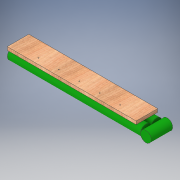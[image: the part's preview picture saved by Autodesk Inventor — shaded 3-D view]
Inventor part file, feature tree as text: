
AUTODESK INVENTOR PART (.ipt)
format: ipt  version: 2018 (Build 220112000, 112)  size: 156,160 bytes
history: native  units: in
note: dims shown in document units (in); Inventor stores cm internally (conversion verified against a paired STEP export)
features: extrude x4, sketch x4
ambient origin geometry x8: Origin, YZ Plane, XZ Plane, XY Plane, X Axis, Y Axis, Z Axis, Center Point
bodies: Solid1 (feature_tree)
feature tree (8):
  extrude  "Extrusion1"  Depth=0.75in
  extrude  "Extrusion2"  Depth=1.25in
  extrude  "Extrusion4"  Depth=1.25in
  extrude  "Extrusion6"  Depth=1.25in
  sketch  "Sketch1"  dims[d0=30.0in d1=0.75in]
  sketch  "Sketch2"  dims[d2=5.0in d3=0.0in d4=1.25in]
  sketch  "Sketch4"  dims[d5=1.25in d6=2.5in]
  sketch  "Sketch5"  dims[d7=31.0in d8=0.0in d13=1.25in d14=5.0in d15=0.0in d16=1.375in d17=5.875in d30=0.2031in d33=4.75in d34=4.75in d35=4.75in d36=4.75in d37=0.75in d38=0.0in]
